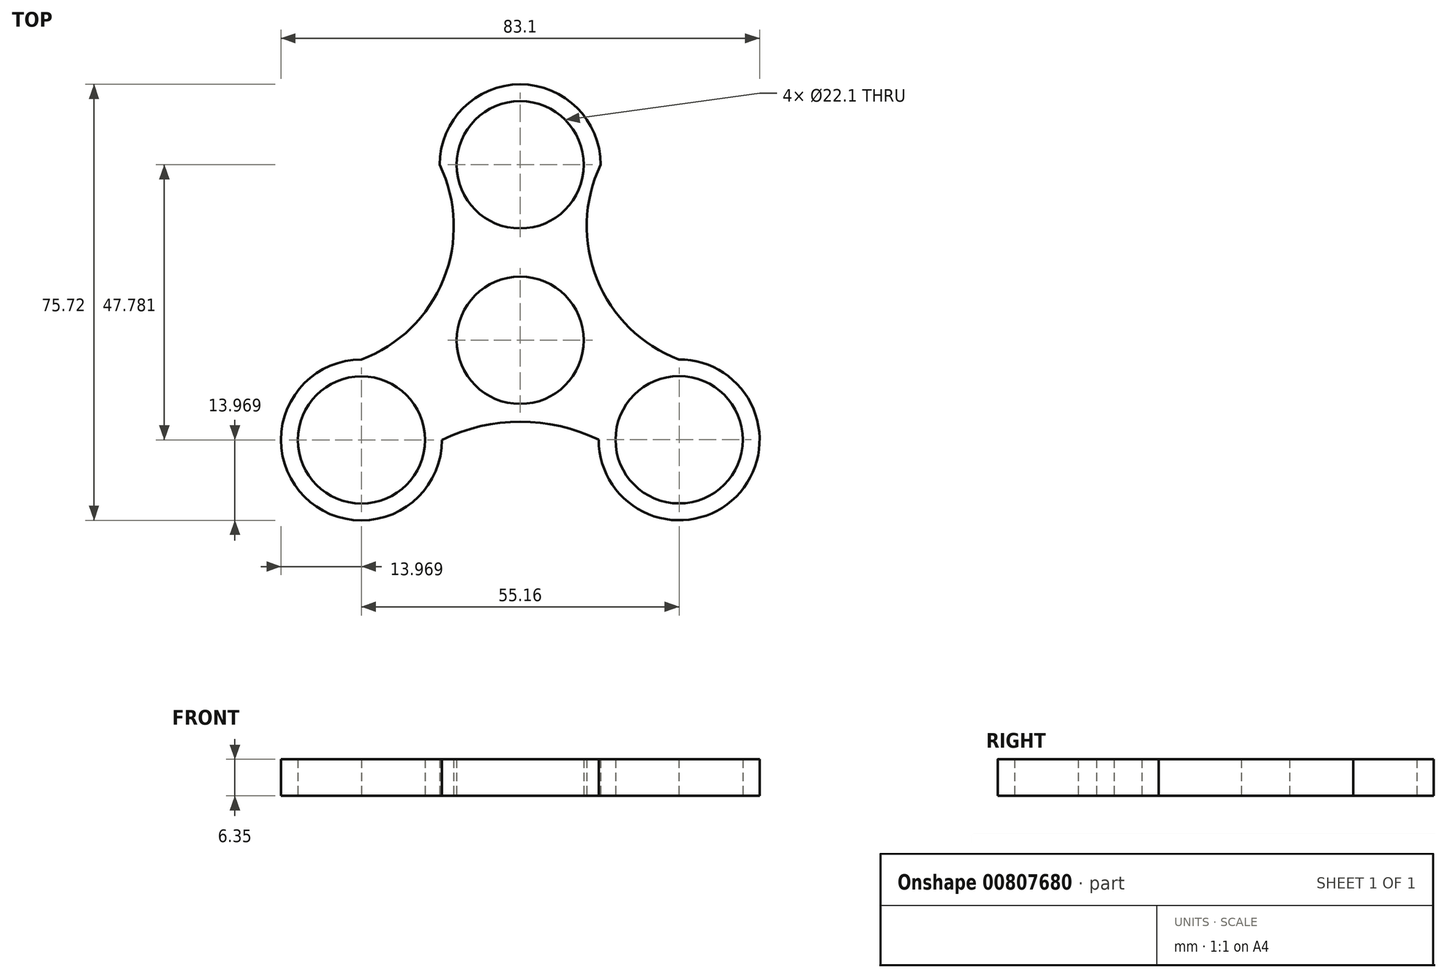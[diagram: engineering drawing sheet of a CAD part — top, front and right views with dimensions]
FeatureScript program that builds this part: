
annotation { "Feature Type Name" : "Feature", "Feature Type Description" : "" }
export const myFeature = defineFeature(function(context is Context, id is Id, definition is map)
    precondition{}
    {
        {
            var Q0;
            Q0=qCreatedBy(makeId("Top.planeOp"),FACE);
            var sketch = newSketch(context, id + "F0", { "sketchPlane" : qUnion([Q0])});
            skCircle(sketch, "E0", {"center": v(0, 0) * mm, "radius": 44.45 * mm});
            skCircle(sketch, "E1", {"center": v(0, 0) * mm, "radius": 11.05 * mm});
            skLineSegment(sketch, "E2", {"start": v(0, 0) * mm, "end": v(0, 30.48) * mm});
            skCircle(sketch, "E3", {"center": v(0, 30.48) * mm, "radius": 11.05 * mm});
            skCircle(sketch, "E4.1.0", {"center": v(-27.56, -17.3) * mm, "radius": 11.05 * mm});
            skCircle(sketch, "E4.2.0", {"center": v(27.6, -17.28) * mm, "radius": 11.05 * mm});
            skPoint(sketch, "E4.center", {"position": v(0.01, -1.37) * mm});
            skCircle(sketch, "E5", {"center": v(0, 30.48) * mm, "radius": 13.97 * mm});
            skCircle(sketch, "E6", {"center": v(27.6, -17.28) * mm, "radius": 13.97 * mm});
            skCircle(sketch, "E7", {"center": v(0, 0) * mm, "radius": 13.97 * mm});
            skCircle(sketch, "E8", {"center": v(-27.56, -17.3) * mm, "radius": 13.97 * mm});
            skArc(sketch, "E9", {"start": v(-27.56, -3.33) * mm, "mid": v(-13.31, 10.58) * mm, "end": v(-13.97, 30.48) * mm});
            skArc(sketch, "E10", {"start": v(13.97, 30.48) * mm, "mid": v(13.33, 10.57) * mm, "end": v(27.6, -3.33) * mm});
            skArc(sketch, "E11", {"start": v(13.63, -17.28) * mm, "mid": v(0.02, -14.14) * mm, "end": v(-13.6, -17.3) * mm});
            skSolve(sketch);
        }
        {
            var Q0;
            {var subQ0=sQuery(id+"F0.wireOp",EDGE,"E8");var subQ1=sQuery(id+"F0.wireOp",EDGE,"E0");var subQ2=makeQuery(id+"F0.imprint","INTERSECT",VERTEX,{"disambiguationData":[OD(0.0)],"derivedFrom":[subQ1,subQ0]});Q0=makeQuery(id+"F0.imprint","IMPRINT",FACE,{"disambiguationData":[TD([[makeQuery(id+"F0.imprint","IMPRINT",EDGE,{"disambiguationData":[TD([[subQ2,-1.0]])],"derivedFrom":subQ1}),-1.0]])]});}
            var Q1;
            {var subQ0=sQuery(id+"F0.wireOp",EDGE,"E6");var subQ1=sQuery(id+"F0.wireOp",EDGE,"E0");var subQ2=makeQuery(id+"F0.imprint","INTERSECT",VERTEX,{"disambiguationData":[OD(0.0)],"derivedFrom":[subQ1,subQ0]});Q1=makeQuery(id+"F0.imprint","IMPRINT",FACE,{"disambiguationData":[TD([[makeQuery(id+"F0.imprint","IMPRINT",EDGE,{"disambiguationData":[TD([[subQ2,-1.0]])],"derivedFrom":subQ1}),-1.0]])]});}
            var Q2;
            Q2=makeQuery(id+"F0.imprint","IMPRINT",FACE,{"disambiguationData":[TD([[makeQuery(id+"F0.imprint","IMPRINT",EDGE,{"derivedFrom":sQuery(id+"F0.wireOp",EDGE,"E4.1.0")}),-1.0]])]});
            var Q3;
            Q3=makeQuery(id+"F0.imprint","IMPRINT",FACE,{"disambiguationData":[TD([[makeQuery(id+"F0.imprint","IMPRINT",EDGE,{"derivedFrom":sQuery(id+"F0.wireOp",EDGE,"E4.2.0")}),-1.0]])]});
            var Q4;
            Q4=makeQuery(id+"F0.imprint","IMPRINT",FACE,{"disambiguationData":[TD([[makeQuery(id+"F0.imprint","IMPRINT",EDGE,{"derivedFrom":sQuery(id+"F0.wireOp",EDGE,"E3")}),-1.0]])]});
            var Q5;
            Q5=makeQuery(id+"F0.imprint","IMPRINT",FACE,{"disambiguationData":[TD([[makeQuery(id+"F0.imprint","IMPRINT",EDGE,{"derivedFrom":sQuery(id+"F0.wireOp",EDGE,"E1")}),-1.0]])]});
            var Q6;
            Q6=makeQuery(id+"F0.imprint","IMPRINT",FACE,{"disambiguationData":[TD([[makeQuery(id+"F0.imprint","IMPRINT",EDGE,{"derivedFrom":sQuery(id+"F0.wireOp",EDGE,"E7")}),-1.0]])]});
            extrude(context, id + "F1", {"entities" : qUnion([Q0, Q1, Q2, Q3, Q4, Q5, Q6]), "depth" : 6.35 * mm, "offsetDistance" : 25.4 * mm});
        }
    });
